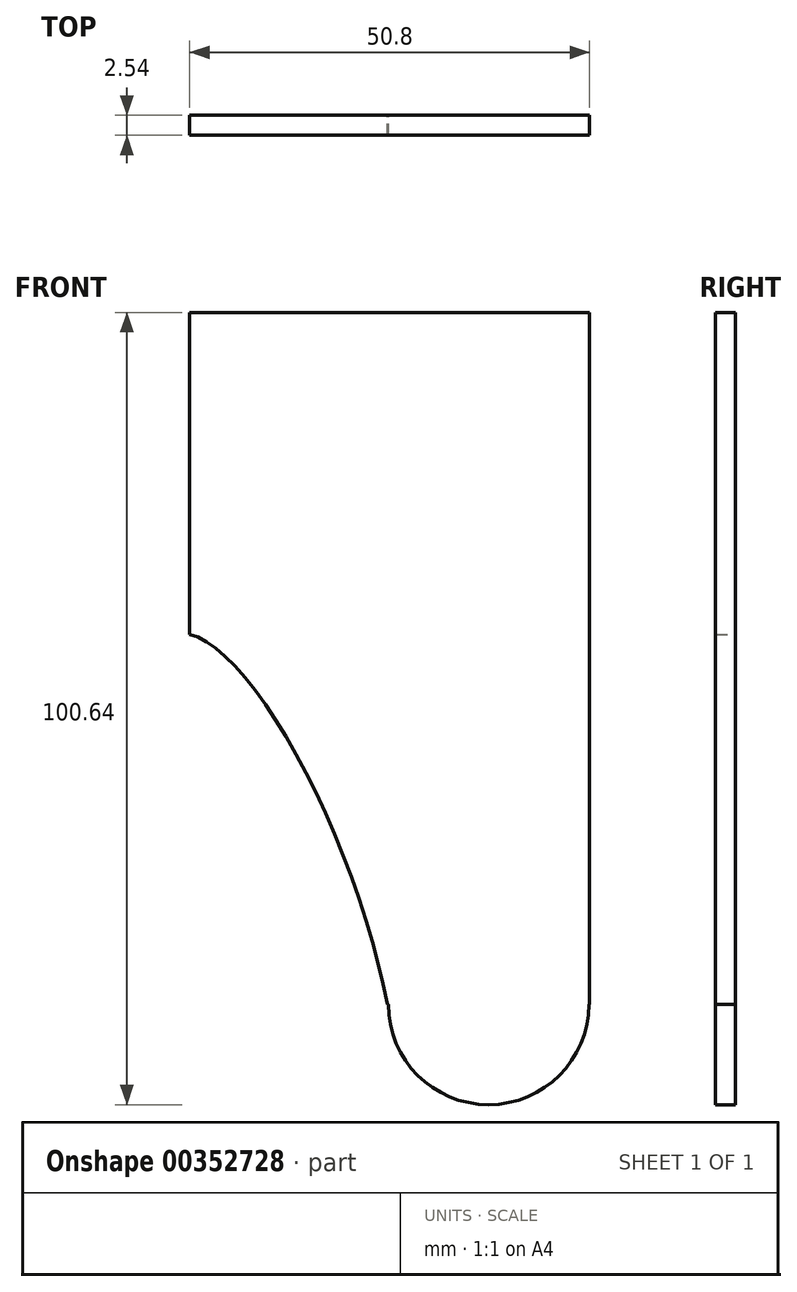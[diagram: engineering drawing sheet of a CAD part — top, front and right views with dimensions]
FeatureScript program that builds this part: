
annotation { "Feature Type Name" : "Feature", "Feature Type Description" : "" }
export const myFeature = defineFeature(function(context is Context, id is Id, definition is map)
    precondition{}
    {
        {
            var Q0;
            Q0=qCreatedBy(makeId("Front.planeOp"),FACE);
            var sketch = newSketch(context, id + "F0", { "sketchPlane" : qUnion([Q0])});
            skLineSegment(sketch, "E0.bottom", {"start": v(-0.3, -43.95) * mm, "end": v(-0.18, -43.95) * mm});
            skLineSegment(sketch, "E0.top", {"start": v(-25.4, 43.95) * mm, "end": v(25.4, 43.95) * mm});
            skLineSegment(sketch, "E0.right", {"start": v(25.4, -43.95) * mm, "end": v(25.4, 43.95) * mm});
            skPoint(sketch, "E0.middle", {"position": v(0, 0) * mm});
            skLineSegment(sketch, "E1.trimOffspring", {"start": v(-25.4, 3.07) * mm, "end": v(-25.4, 43.95) * mm});
            skPoint(sketch, "E2.orphan", {"position": v(-25.4, -43.95) * mm});
            skEllipticalArc(sketch, "E3.trimOffspring", {});
            skArc(sketch, "E4", {"start": v(-0.18, -43.95) * mm, "mid": v(12.55, -56.69) * mm, "end": v(25.29, -43.95) * mm});
            skLineSegment(sketch, "E5.trimOffspring", {"start": v(25.29, -43.95) * mm, "end": v(25.4, -43.95) * mm});
            const initialGuessF0  = {"E3.trimOffspring": [-0.015096666411535448, -0.030419933969172315, 0.35112346778557313, -0.9363291677451011, 0.03570075654183053, 0.010515697738705978, 1.0465974998699268, 2.9394498417662684]};
            skSetInitialGuess(sketch, initialGuessF0);
            skSolve(sketch);
        }
        {
            var Q0;
            Q0=makeQuery(id+"F0.imprint","IMPRINT",FACE,{"disambiguationData":[TD([[makeQuery(id+"F0.imprint","IMPRINT",EDGE,{"derivedFrom":sQuery(id+"F0.wireOp",EDGE,"E0.bottom")}),1.0]])]});
            extrude(context, id + "F1", {"entities" : qUnion([Q0]), "depth" : 2.54 * mm});
        }
    });
